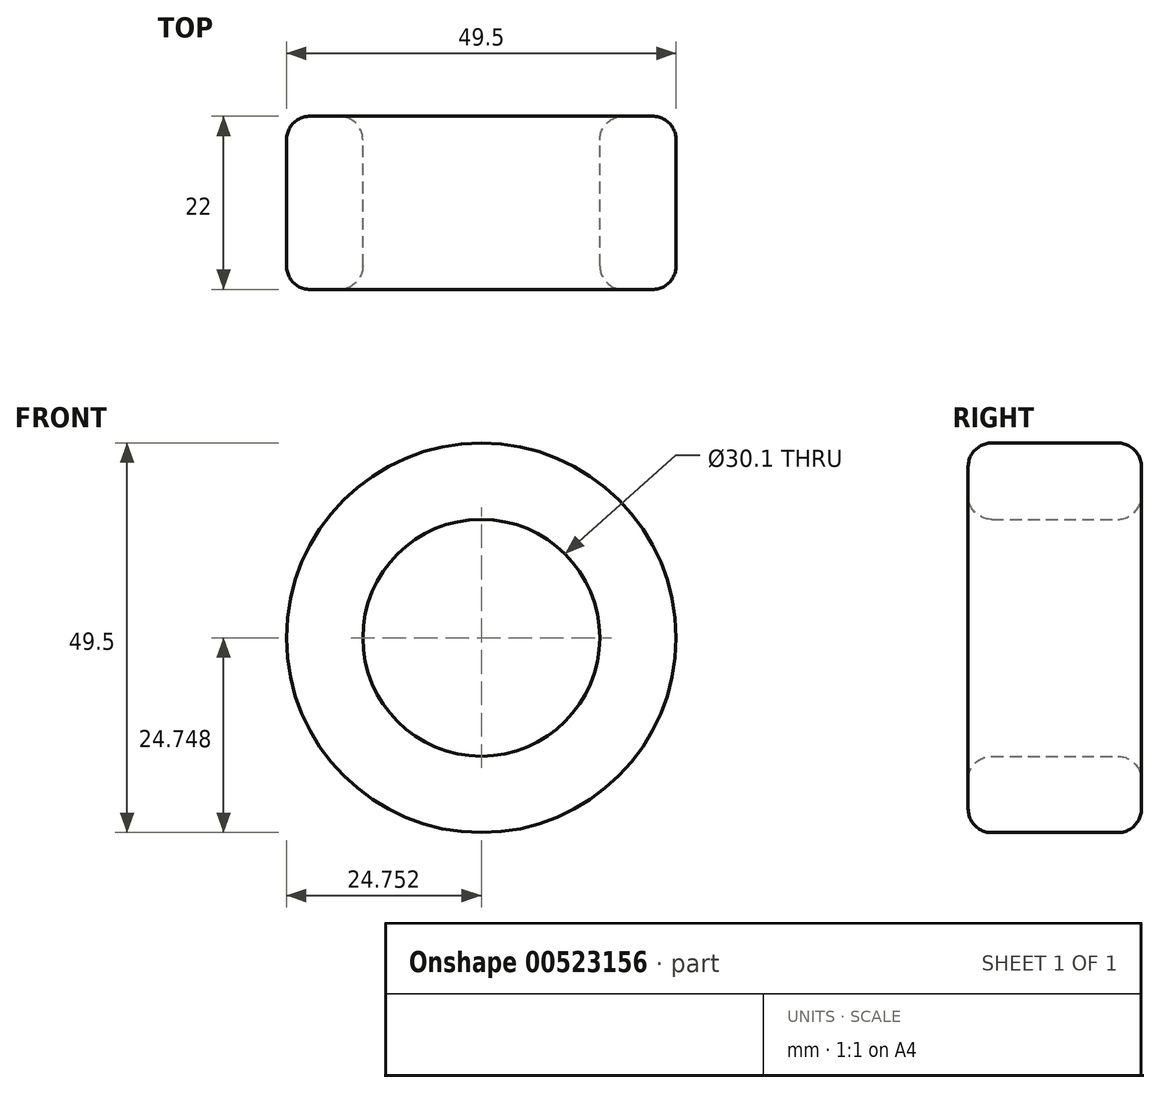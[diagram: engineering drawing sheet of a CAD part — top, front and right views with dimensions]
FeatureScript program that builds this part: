
annotation { "Feature Type Name" : "Feature", "Feature Type Description" : "" }
export const myFeature = defineFeature(function(context is Context, id is Id, definition is map)
    precondition{}
    {
        {
            var Q0;
            Q0=qCreatedBy(makeId("Front.planeOp"),FACE);
            var sketch = newSketch(context, id + "F0", { "sketchPlane" : qUnion([Q0])});
            skCircle(sketch, "E0", {"center": v(-54.1, 43.04) * mm, "radius": 628.65 * mm});
            skCircle(sketch, "E1", {"center": v(-48.68, 43.57) * mm, "radius": 24.75 * mm});
            skCircle(sketch, "E2", {"center": v(-48.68, 43.57) * mm, "radius": 15.05 * mm});
            skSolve(sketch);
        }
        {
            var Q0;
            Q0=makeQuery(id+"F0.imprint","IMPRINT",FACE,{"disambiguationData":[TD([[makeQuery(id+"F0.imprint","IMPRINT",EDGE,{"derivedFrom":sQuery(id+"F0.wireOp",EDGE,"E1")}),1.0]])]});
            extrude(context, id + "F1", {"entities" : qUnion([Q0]), "depth" : 22 * mm, "offsetDistance" : 25 * mm});
        }
        {
            var Q0;
            Q0=makeQuery(id+"F1.opExtrude","CAP_EDGE",EDGE,{"disambiguationData":[OSD([sQuery(id+"F0.wireOp",EDGE,"E1")])],"isStart":false});
            var Q1;
            Q1=makeQuery(id+"F1.opExtrude","CAP_EDGE",EDGE,{"disambiguationData":[OSD([sQuery(id+"F0.wireOp",EDGE,"E1")])],"isStart":true});
            var Q2;
            Q2=makeQuery(id+"F1.opExtrude","CAP_EDGE",EDGE,{"disambiguationData":[OSD([sQuery(id+"F0.wireOp",EDGE,"E2")])],"isStart":false});
            var Q3;
            Q3=makeQuery(id+"F1.opExtrude","CAP_EDGE",EDGE,{"disambiguationData":[OSD([sQuery(id+"F0.wireOp",EDGE,"E2")])],"isStart":true});
            fillet(context, id + "F2", {"entities" : qUnion([Q0, Q1, Q2, Q3]), "radius" : 3 * mm, "tangentPropagation" : true, "allowEdgeOverflow" : false});
        }
    });
